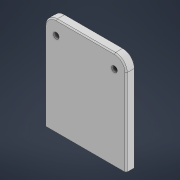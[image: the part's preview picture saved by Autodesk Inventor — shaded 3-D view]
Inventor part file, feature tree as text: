
AUTODESK INVENTOR PART (.ipt)
format: ipt  version: 2021 (Build 250183000, 183)  size: 120,320 bytes
history: native  units: mm
features: sketch x2, extrude x1, fillet x1, hole x1, chamfer x1
ambient origin geometry x8: Origin, YZ Plane, XZ Plane, XY Plane, X Axis, Y Axis, Z Axis, Center Point
bodies: Solid1 (feature_tree)
feature tree (6):
  extrude  "Extrusion1"  Depth=35.0mm
  fillet  "Fillet1"  Radius=84.0mm
  hole  "Hole1"  [1 undecoded]
  chamfer  "Chamfer1"  Distance=70.0mm
  sketch  "Sketch1"  dims[d0=70.0mm d1=35.0mm d2=84.0mm]
  sketch  "Sketch2"  dims[d3=8.0mm d4=0.0mm d5=10.0mm d6=70.0mm d9=50.0mm d10=0.0mm d11=10.0mm d13=72.0mm d14=5.0mm d15=6.0mm d16=4.0mm d17=2.0mm d18=90.0deg d19=8.0mm d20=0.0mm d21=1.0mm d22=2.0mm d23=45.0deg]
note: 1 required parameter value undecoded (feature->parameter linkage not recoverable at this tier; creation-order binding heuristic only, values carry confidence <= 0.55)
